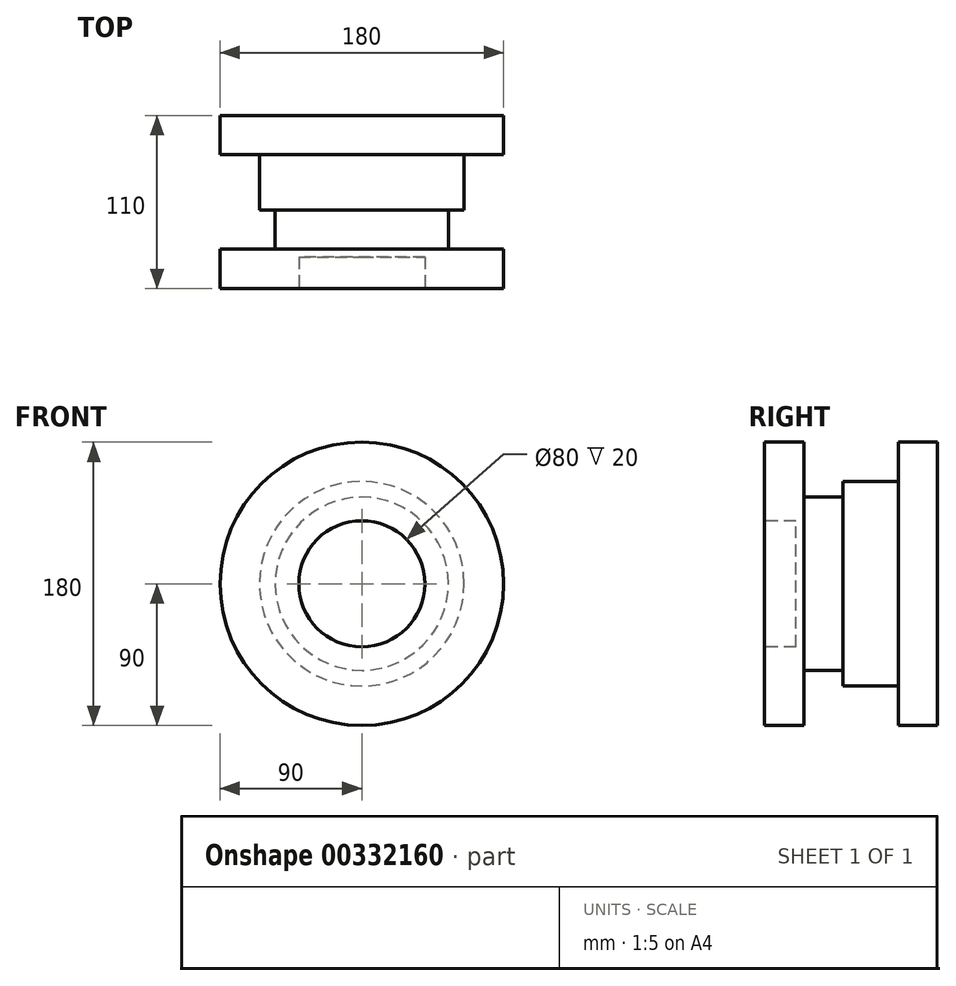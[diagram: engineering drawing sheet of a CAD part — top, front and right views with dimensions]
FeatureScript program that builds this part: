
annotation { "Feature Type Name" : "Feature", "Feature Type Description" : "" }
export const myFeature = defineFeature(function(context is Context, id is Id, definition is map)
    precondition{}
    {
        {
            var Q0;
            Q0=qCreatedBy(makeId("Top.planeOp"),FACE);
            var sketch = newSketch(context, id + "F0", { "sketchPlane" : qUnion([Q0])});
            skLineSegment(sketch, "E0", {"start": v(0, 0) * mm, "end": v(0, 110) * mm});
            skLineSegment(sketch, "E1", {"start": v(0, 110) * mm, "end": v(90, 110) * mm});
            skLineSegment(sketch, "E2", {"start": v(90, 110) * mm, "end": v(90, 85) * mm});
            skLineSegment(sketch, "E3", {"start": v(90, 85) * mm, "end": v(65, 85) * mm});
            skLineSegment(sketch, "E4", {"start": v(65, 85) * mm, "end": v(65, 50) * mm});
            skLineSegment(sketch, "E5", {"start": v(65, 50) * mm, "end": v(55, 50) * mm});
            skLineSegment(sketch, "E6", {"start": v(55, 50) * mm, "end": v(55, 25) * mm});
            skLineSegment(sketch, "E7", {"start": v(55, 25) * mm, "end": v(90, 25) * mm});
            skLineSegment(sketch, "E8", {"start": v(90, 25) * mm, "end": v(90, 0) * mm});
            skLineSegment(sketch, "E9", {"start": v(90, 0) * mm, "end": v(0, 0) * mm});
            skSolve(sketch);
        }
        {
            var Q0;
            Q0=makeQuery(id+"F0.imprint","IMPRINT",FACE,{"disambiguationData":[TD([[makeQuery(id+"F0.imprint","IMPRINT",EDGE,{"derivedFrom":sQuery(id+"F0.wireOp",EDGE,"E0")}),-1.0]])]});
            var Q1;
            Q1=sQuery(id+"F0.wireOp",EDGE,"E0");
            revolve(context, id + "F1", {"entities" : qUnion([Q0]), "axis" : qUnion([Q1]), "revolveType" : RevolveType.FULL});
        }
        {
            var Q0;
            Q0=makeQuery(id+"F1.opRevolve","SWEPT_FACE",FACE,{"disambiguationData":[OSD([sQuery(id+"F0.wireOp",EDGE,"E9")])]});
            var sketch = newSketch(context, id + "F2", { "sketchPlane" : qUnion([Q0])});
            skCircle(sketch, "E10", {"center": v(0, 0) * mm, "radius": 40 * mm});
            skSolve(sketch);
        }
        {
            var Q0;
            Q0=makeQuery(id+"F2.imprint","IMPRINT",FACE,{"disambiguationData":[TD([[makeQuery(id+"F2.imprint","IMPRINT",EDGE,{"derivedFrom":sQuery(id+"F2.wireOp",EDGE,"E10")}),1.0]])]});
            extrude(context, id + "F3", {"entities" : qUnion([Q0]), "operationType" : NewBodyOperationType.REMOVE, "endBound" : BoundingType.SYMMETRIC, "oppositeDirection" : true, "depth" : 40 * mm});
        }
    });
